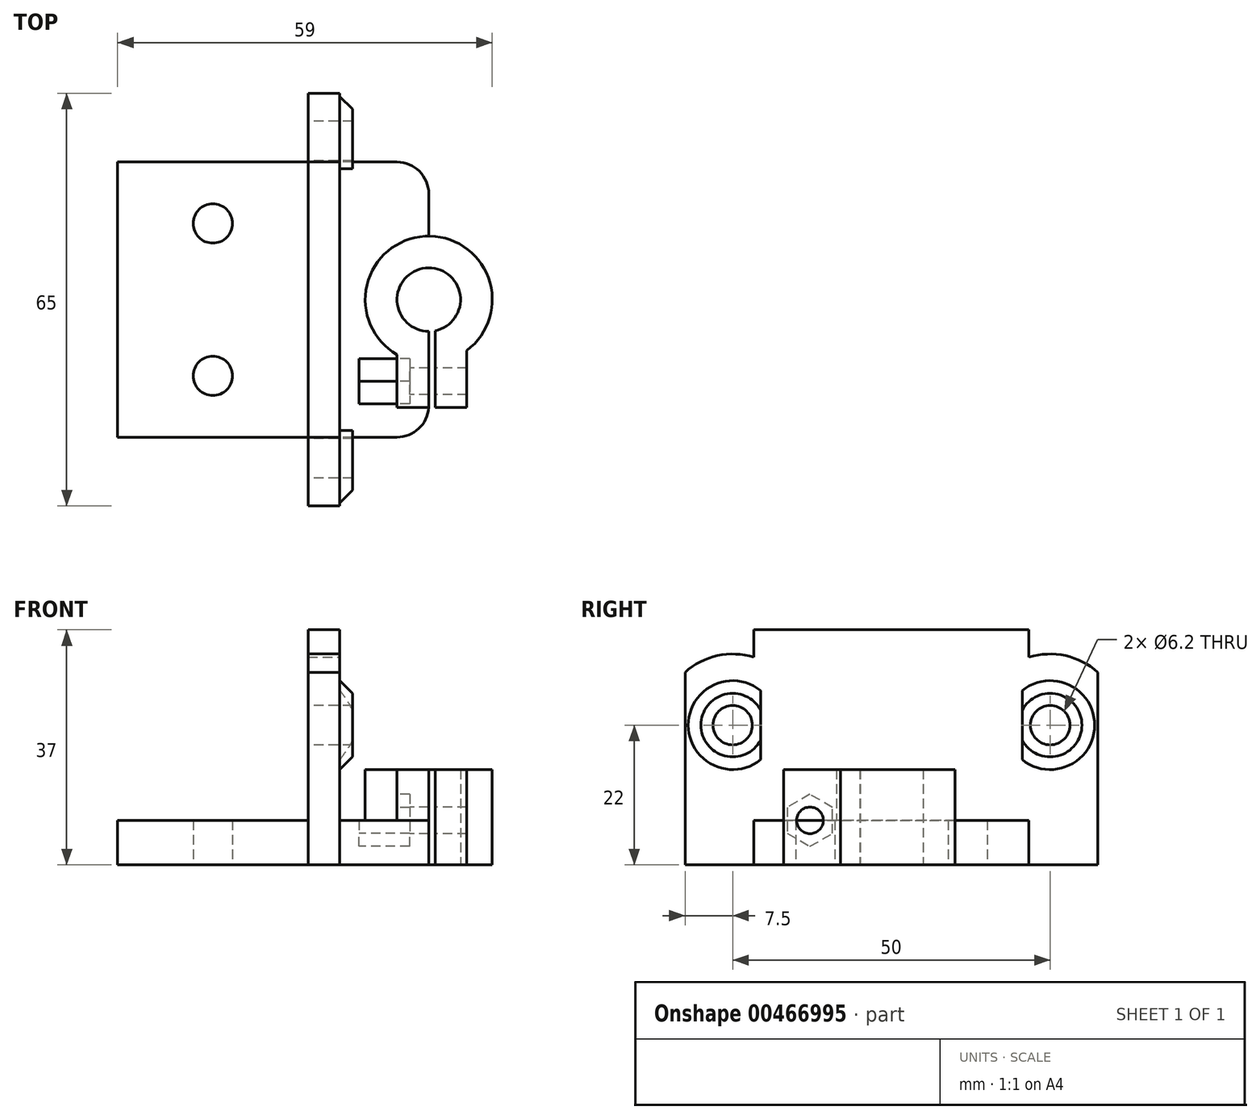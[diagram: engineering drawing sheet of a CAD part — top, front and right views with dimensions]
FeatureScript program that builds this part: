
annotation { "Feature Type Name" : "Feature", "Feature Type Description" : "" }
export const myFeature = defineFeature(function(context is Context, id is Id, definition is map)
    precondition{}
    {
        {
            var Q0;
            Q0=qCreatedBy(makeId("Top.planeOp"),FACE);
            var sketch = newSketch(context, id + "F0", { "sketchPlane" : qUnion([Q0])});
            skArc(sketch, "E0", {"start": v(1, -4.9) * mm, "mid": v(-0.5, 4.97) * mm, "end": v(0, -5) * mm});
            skArc(sketch, "E1", {"start": v(6, -8) * mm, "mid": v(-0.6, 9.98) * mm, "end": v(-5, -8.66) * mm});
            skCircle(sketch, "E2", {"center": v(-34, 12) * mm, "radius": 3.1 * mm});
            skCircle(sketch, "E3.MirrorC", {"center": v(-34, -12) * mm, "radius": 3.1 * mm});
            skLineSegment(sketch, "E4", {"start": v(0, 10) * mm, "end": v(0, 16.66) * mm});
            skLineSegment(sketch, "E5", {"start": v(-5, 21.66) * mm, "end": v(-49, 21.66) * mm});
            skLineSegment(sketch, "E6", {"start": v(-49, 21.66) * mm, "end": v(-49, 0) * mm});
            skPoint(sketch, "E7.visualSharp", {"position": v(0, 21.66) * mm});
            skArc(sketch, "E7.filletArc", {"start": v(0, 16.66) * mm, "mid": v(-1.46, 20.2) * mm, "end": v(-5, 21.66) * mm});
            skLineSegment(sketch, "E8.MirrorCS", {"start": v(-49, -21.66) * mm, "end": v(-49, 0) * mm});
            skLineSegment(sketch, "E9.MirrorCS", {"start": v(-5, -21.66) * mm, "end": v(-49, -21.66) * mm});
            skArc(sketch, "E10.MirrorCS", {"start": v(0, -16.66) * mm, "mid": v(-1.46, -20.2) * mm, "end": v(-5, -21.66) * mm});
            skLineSegment(sketch, "E11.MirrorCS", {"start": v(0, -10) * mm, "end": v(0, -16.66) * mm});
            skLineSegment(sketch, "E12", {"start": v(0, -5) * mm, "end": v(0, -10) * mm});
            skLineSegment(sketch, "E13", {"start": v(1, -9.95) * mm, "end": v(1, -4.9) * mm});
            skLineSegment(sketch, "E14", {"start": v(1, -9.95) * mm, "end": v(1, -17) * mm});
            skLineSegment(sketch, "E15", {"start": v(1, -17) * mm, "end": v(6, -17) * mm});
            skLineSegment(sketch, "E16", {"start": v(6, -17) * mm, "end": v(6, -8) * mm});
            skLineSegment(sketch, "E17", {"start": v(-5, -17) * mm, "end": v(-5, -8.66) * mm});
            skLineSegment(sketch, "E18", {"start": v(0, -17) * mm, "end": v(-5, -17) * mm});
            skSolve(sketch);
        }
        {
            var Q0;
            Q0=makeQuery(id+"F0.imprint","IMPRINT",FACE,{"disambiguationData":[TD([[makeQuery(id+"F0.imprint","IMPRINT",EDGE,{"derivedFrom":sQuery(id+"F0.wireOp",EDGE,"E2")}),-1.0]])]});
            extrude(context, id + "F1", {"entities" : qUnion([Q0]), "depth" : 7 * mm});
        }
        {
            var Q0;
            Q0=makeQuery(id+"F0.imprint","IMPRINT",FACE,{"disambiguationData":[TD([[makeQuery(id+"F0.imprint","IMPRINT",EDGE,{"derivedFrom":sQuery(id+"F0.wireOp",EDGE,"E0")}),-1.0]])]});
            extrude(context, id + "F2", {"entities" : qUnion([Q0]), "operationType" : NewBodyOperationType.ADD, "depth" : 15 * mm});
        }
        {
            var Q0;
            Q0=makeQuery(id+"F2.opExtrude","SWEPT_FACE",FACE,{"disambiguationData":[OSD([sQuery(id+"F0.wireOp",EDGE,"E17")])]});
            var sketch = newSketch(context, id + "F3", { "sketchPlane" : qUnion([Q0])});
            skCircle(sketch, "E19.cCircle", {"center": v(12.83, 7) * mm, "radius": 3.55 * mm, "construction": true});
            skLineSegment(sketch, "E19.0", {"start": v(16.38, 9.05) * mm, "end": v(16.38, 4.95) * mm});
            skLineSegment(sketch, "E19.1", {"start": v(16.38, 4.95) * mm, "end": v(12.83, 2.9) * mm});
            skLineSegment(sketch, "E19.2", {"start": v(12.83, 2.9) * mm, "end": v(9.28, 4.95) * mm});
            skLineSegment(sketch, "E19.3", {"start": v(9.28, 4.95) * mm, "end": v(9.28, 9.05) * mm});
            skLineSegment(sketch, "E19.4", {"start": v(9.28, 9.05) * mm, "end": v(12.83, 11.1) * mm});
            skLineSegment(sketch, "E19.5", {"start": v(12.83, 11.1) * mm, "end": v(16.38, 9.05) * mm});
            skPoint(sketch, "E19.0.midPoint", {"position": v(16.38, 7) * mm});
            skSolve(sketch);
        }
        {
            var Q0;
            Q0 = qSketchRegion(id + "F3", true);
            extrude(context, id + "F4", {"entities" : qUnion([Q0]), "operationType" : NewBodyOperationType.REMOVE, "oppositeDirection" : true, "depth" : 2 * mm, "hasSecondDirection" : true, "secondDirectionOppositeDirection" : false, "secondDirectionDepth" : 6 * mm});
        }
        {
            var Q0;
            Q0=makeQuery(id+"F2.opExtrude","SWEPT_FACE",FACE,{"disambiguationData":[OSD([sQuery(id+"F0.wireOp",EDGE,"E17")])]});
            var sketch = newSketch(context, id + "F5", { "sketchPlane" : qUnion([Q0])});
            skCircle(sketch, "E20", {"center": v(12.83, 7) * mm, "radius": 2.1 * mm});
            skSolve(sketch);
        }
        {
            var Q0;
            Q0 = qSketchRegion(id + "F5", true);
            extrude(context, id + "F6", {"entities" : qUnion([Q0]), "operationType" : NewBodyOperationType.REMOVE, "oppositeDirection" : true, "depth" : 25 * mm});
        }
        {
            var Q0;
            Q0=makeQuery(id+"F1.opExtrude","CAP_FACE",FACE,{"disambiguationData":[OSD([sQuery(id+"F0.wireOp",EDGE,"E1"),sQuery(id+"F0.wireOp",EDGE,"E2"),sQuery(id+"F0.wireOp",EDGE,"E3.MirrorC"),sQuery(id+"F0.wireOp",EDGE,"E4"),sQuery(id+"F0.wireOp",EDGE,"E5"),sQuery(id+"F0.wireOp",EDGE,"E6"),sQuery(id+"F0.wireOp",EDGE,"E7.filletArc"),sQuery(id+"F0.wireOp",EDGE,"E8.MirrorCS"),sQuery(id+"F0.wireOp",EDGE,"E9.MirrorCS"),sQuery(id+"F0.wireOp",EDGE,"E10.MirrorCS"),sQuery(id+"F0.wireOp",EDGE,"E17"),sQuery(id+"F0.wireOp",EDGE,"E18")])],"isStart":false});
            var sketch = newSketch(context, id + "F7", { "sketchPlane" : qUnion([Q0])});
            skLineSegment(sketch, "E21", {"start": v(-19, 21.66) * mm, "end": v(-19, -21.66) * mm});
            skLineSegment(sketch, "E22", {"start": v(-14, -21.66) * mm, "end": v(-14, 21.66) * mm});
            skLineSegment(sketch, "E23", {"start": v(-14, 21.66) * mm, "end": v(-14, 32.5) * mm});
            skLineSegment(sketch, "E24", {"start": v(-14, 32.5) * mm, "end": v(-19, 32.5) * mm});
            skLineSegment(sketch, "E25", {"start": v(-19, 32.5) * mm, "end": v(-19, 21.66) * mm});
            skLineSegment(sketch, "E26.MirrorCS", {"start": v(-14, -32.5) * mm, "end": v(-19, -32.5) * mm});
            skLineSegment(sketch, "E27.MirrorCS", {"start": v(-14, -21.66) * mm, "end": v(-14, -32.5) * mm});
            skLineSegment(sketch, "E28.MirrorCS", {"start": v(-19, -32.5) * mm, "end": v(-19, -21.66) * mm});
            skPoint(sketch, "E29.MirrorCS.start.orphan", {"position": v(-14, -21.66) * mm});
            skSolve(sketch);
        }
        {
            var Q0;
            Q0 = qSketchRegion(id + "F7", true);
            extrude(context, id + "F8", {"entities" : qUnion([Q0]), "operationType" : NewBodyOperationType.ADD, "depth" : 30 * mm});
        }
        {
            var Q0;
            Q0 = qSketchRegion(id + "F7", true);
            var Q1;
            {var subQ0=sQuery(id+"F0.wireOp",EDGE,"E18");var subQ1=sQuery(id+"F0.wireOp",EDGE,"E17");var subQ2=sQuery(id+"F0.wireOp",EDGE,"E10.MirrorCS");var subQ3=sQuery(id+"F0.wireOp",EDGE,"E1");Q1=makeQuery(id+"F2.boolean.opBoolean","MERGE",FACE,{"derivedFrom":[makeQuery(id+"F1.opExtrude","CAP_FACE",FACE,{"disambiguationData":[OSD([subQ3,sQuery(id+"F0.wireOp",EDGE,"E2"),sQuery(id+"F0.wireOp",EDGE,"E3.MirrorC"),sQuery(id+"F0.wireOp",EDGE,"E4"),sQuery(id+"F0.wireOp",EDGE,"E5"),sQuery(id+"F0.wireOp",EDGE,"E6"),sQuery(id+"F0.wireOp",EDGE,"E7.filletArc"),sQuery(id+"F0.wireOp",EDGE,"E8.MirrorCS"),sQuery(id+"F0.wireOp",EDGE,"E9.MirrorCS"),subQ2,subQ1,subQ0])],"isStart":true}),makeQuery(id+"F2.opExtrude","CAP_FACE",FACE,{"disambiguationData":[OSD([sQuery(id+"F0.wireOp",EDGE,"E0"),subQ3,subQ2,sQuery(id+"F0.wireOp",EDGE,"E11.MirrorCS"),sQuery(id+"F0.wireOp",EDGE,"E12"),sQuery(id+"F0.wireOp",EDGE,"E13"),sQuery(id+"F0.wireOp",EDGE,"E14"),sQuery(id+"F0.wireOp",EDGE,"E15"),sQuery(id+"F0.wireOp",EDGE,"E16"),subQ1,subQ0])],"isStart":true})]});}
            extrude(context, id + "F9", {"entities" : qUnion([Q0]), "operationType" : NewBodyOperationType.ADD, "depth" : 25 * mm, "hasSecondDirection" : true, "secondDirectionBound" : SecondDirectionBoundingType.UP_TO_SURFACE, "secondDirectionOppositeDirection" : true, "secondDirectionBoundEntityFace" : qUnion([Q1]), "secondDirectionDepth" : 25 * mm});
        }
        {
            var Q0;
            Q0=makeQuery(id+"F8.opExtrude","SWEPT_FACE",FACE,{"disambiguationData":[OSD([sQuery(id+"F7.wireOp",EDGE,"E21")])]});
            var sketch = newSketch(context, id + "F10", { "sketchPlane" : qUnion([Q0])});
            skCircle(sketch, "E30", {"center": v(-25, 22) * mm, "radius": 3.1 * mm});
            skCircle(sketch, "E31.MirrorC", {"center": v(25, 22) * mm, "radius": 3.1 * mm});
            skLineSegment(sketch, "E32", {"start": v(20, 43.23) * mm, "end": v(20, 10) * mm, "construction": true});
            skSolve(sketch);
        }
        {
            var Q0;
            Q0 = qSketchRegion(id + "F10", true);
            extrude(context, id + "F11", {"entities" : qUnion([Q0]), "operationType" : NewBodyOperationType.REMOVE, "oppositeDirection" : true, "depth" : 25 * mm});
        }
        {
            var Q0;
            {var subQ0=sQuery(id+"F7.wireOp",EDGE,"E28.MirrorCS");var subQ1=sQuery(id+"F7.wireOp",EDGE,"E25");var subQ2=sQuery(id+"F7.wireOp",EDGE,"E21");Q0=makeQuery(id+"F9.boolean.opBoolean","MERGE",FACE,{"derivedFrom":[makeQuery(id+"F8.opExtrude","SWEPT_FACE",FACE,{"disambiguationData":[OSD([subQ2,subQ1,subQ0])]}),makeQuery(id+"F9.opExtrude","SWEPT_FACE",FACE,{"disambiguationData":[OSD([subQ2,subQ1,subQ0])]})]});}
            var sketch = newSketch(context, id + "F12", { "sketchPlane" : qUnion([Q0])});
            skLineSegment(sketch, "E33", {"start": v(20, 49.57) * mm, "end": v(20, 11.1) * mm, "construction": true});
            skCircle(sketch, "E34", {"center": v(25, 22) * mm, "radius": 5 * mm});
            skCircle(sketch, "E35.MirrorC", {"center": v(-25, 22) * mm, "radius": 5 * mm});
            skCircle(sketch, "E36", {"center": v(25, 22) * mm, "radius": 3.1 * mm});
            skCircle(sketch, "E37.MirrorC", {"center": v(-25, 22) * mm, "radius": 3.1 * mm});
            skSolve(sketch);
        }
        {
            var Q0;
            Q0 = qSketchRegion(id + "F12", true);
            extrude(context, id + "F13", {"entities" : qUnion([Q0]), "operationType" : NewBodyOperationType.ADD, "oppositeDirection" : true, "depth" : 7 * mm});
        }
        {
            var Q0;
            {var subQ0=sQuery(id+"F7.wireOp",EDGE,"E27.MirrorCS");var subQ1=sQuery(id+"F7.wireOp",EDGE,"E23");var subQ2=sQuery(id+"F7.wireOp",EDGE,"E22");Q0=makeQuery(id+"F13.boolean.opBoolean","INTERSECT",EDGE,{"derivedFrom":[makeQuery(id+"F9.boolean.opBoolean","MERGE",FACE,{"derivedFrom":[makeQuery(id+"F8.opExtrude","SWEPT_FACE",FACE,{"disambiguationData":[OSD([subQ2,subQ1,subQ0])]}),makeQuery(id+"F9.opExtrude","SWEPT_FACE",FACE,{"disambiguationData":[OSD([subQ2,subQ1,subQ0])]})]}),makeQuery(id+"F13.opExtrude","SWEPT_FACE",FACE,{"disambiguationData":[OSD([sQuery(id+"F12.wireOp",EDGE,"E35.MirrorC")])]})]});}
            var Q1;
            {var subQ0=sQuery(id+"F7.wireOp",EDGE,"E27.MirrorCS");var subQ1=sQuery(id+"F7.wireOp",EDGE,"E23");var subQ2=sQuery(id+"F7.wireOp",EDGE,"E22");Q1=makeQuery(id+"F13.boolean.opBoolean","INTERSECT",EDGE,{"derivedFrom":[makeQuery(id+"F9.boolean.opBoolean","MERGE",FACE,{"derivedFrom":[makeQuery(id+"F8.opExtrude","SWEPT_FACE",FACE,{"disambiguationData":[OSD([subQ2,subQ1,subQ0])]}),makeQuery(id+"F9.opExtrude","SWEPT_FACE",FACE,{"disambiguationData":[OSD([subQ2,subQ1,subQ0])]})]}),makeQuery(id+"F13.opExtrude","SWEPT_FACE",FACE,{"disambiguationData":[OSD([sQuery(id+"F12.wireOp",EDGE,"E34")])]})]});}
            chamfer(context, id + "F14", {"entities" : qUnion([Q0, Q1]), "width" : 2 * mm, "tangentPropagation" : true});
        }
        {
            var Q0;
            {var subQ0=sQuery(id+"F7.wireOp",EDGE,"E27.MirrorCS");var subQ1=sQuery(id+"F7.wireOp",EDGE,"E23");var subQ2=sQuery(id+"F7.wireOp",EDGE,"E22");Q0=makeQuery(id+"F9.boolean.opBoolean","MERGE",FACE,{"derivedFrom":[makeQuery(id+"F8.opExtrude","SWEPT_FACE",FACE,{"disambiguationData":[OSD([subQ2,subQ1,subQ0])]}),makeQuery(id+"F9.opExtrude","SWEPT_FACE",FACE,{"disambiguationData":[OSD([subQ2,subQ1,subQ0])]})]});}
            var sketch = newSketch(context, id + "F15", { "sketchPlane" : qUnion([Q0])});
            skLineSegment(sketch, "E38", {"start": v(20.6, 14.46) * mm, "end": v(20.6, 30.1) * mm});
            skLineSegment(sketch, "E39", {"start": v(20.6, 30.1) * mm, "end": v(17.14, 30.1) * mm});
            skLineSegment(sketch, "E40", {"start": v(17.14, 30.1) * mm, "end": v(17.14, 14.46) * mm});
            skLineSegment(sketch, "E41", {"start": v(17.14, 14.46) * mm, "end": v(20.6, 14.46) * mm});
            skLineSegment(sketch, "E42.MirrorCS", {"start": v(-20.6, 30.1) * mm, "end": v(-17.14, 30.1) * mm});
            skLineSegment(sketch, "E43.MirrorCS", {"start": v(-17.14, 14.46) * mm, "end": v(-20.6, 14.46) * mm});
            skLineSegment(sketch, "E44.MirrorCS", {"start": v(-17.14, 30.1) * mm, "end": v(-17.14, 14.46) * mm});
            skLineSegment(sketch, "E45.MirrorCS", {"start": v(-20.6, 14.46) * mm, "end": v(-20.6, 30.1) * mm});
            skSolve(sketch);
        }
        {
            var Q0;
            Q0 = qSketchRegion(id + "F15", true);
            extrude(context, id + "F16", {"entities" : qUnion([Q0]), "operationType" : NewBodyOperationType.REMOVE, "depth" : 25 * mm});
        }
        {
            var Q0;
            {var subQ0=sQuery(id+"F7.wireOp",EDGE,"E27.MirrorCS");var subQ1=sQuery(id+"F7.wireOp",EDGE,"E23");var subQ2=sQuery(id+"F7.wireOp",EDGE,"E22");Q0=makeQuery(id+"F16.boolean.opBoolean","MERGE",FACE,{"derivedFrom":[makeQuery(id+"F9.boolean.opBoolean","MERGE",FACE,{"derivedFrom":[makeQuery(id+"F8.opExtrude","SWEPT_FACE",FACE,{"disambiguationData":[OSD([subQ2,subQ1,subQ0])]}),makeQuery(id+"F9.opExtrude","SWEPT_FACE",FACE,{"disambiguationData":[OSD([subQ2,subQ1,subQ0])]})]}),makeQuery(id+"F16.opExtrude","CAP_FACE",FACE,{"disambiguationData":[OSD([sQuery(id+"F15.wireOp",EDGE,"E38"),sQuery(id+"F15.wireOp",EDGE,"E39"),sQuery(id+"F15.wireOp",EDGE,"E40"),sQuery(id+"F15.wireOp",EDGE,"E41")])],"isStart":true}),makeQuery(id+"F16.opExtrude","CAP_FACE",FACE,{"disambiguationData":[OSD([sQuery(id+"F15.wireOp",EDGE,"E42.MirrorCS"),sQuery(id+"F15.wireOp",EDGE,"E43.MirrorCS"),sQuery(id+"F15.wireOp",EDGE,"E44.MirrorCS"),sQuery(id+"F15.wireOp",EDGE,"E45.MirrorCS")])],"isStart":true})]});}
            var sketch = newSketch(context, id + "F17", { "sketchPlane" : qUnion([Q0])});
            skLineSegment(sketch, "E46", {"start": v(21.66, 32.69) * mm, "end": v(21.66, 43.29) * mm});
            skArc(sketch, "E47", {"start": v(32.5, 30.31) * mm, "mid": v(27.4, 32.94) * mm, "end": v(21.66, 32.69) * mm});
            skLineSegment(sketch, "E48", {"start": v(32.5, 30.31) * mm, "end": v(32.5, 43.29) * mm});
            skLineSegment(sketch, "E49", {"start": v(32.5, 43.29) * mm, "end": v(21.66, 43.29) * mm});
            skPoint(sketch, "E50.orphan", {"position": v(21.66, 30.93) * mm});
            skPoint(sketch, "E51.MirrorP", {"position": v(-21.66, 30.93) * mm});
            skLineSegment(sketch, "E52.MirrorCS", {"start": v(-21.66, 32.69) * mm, "end": v(-21.66, 43.29) * mm});
            skArc(sketch, "E53.MirrorCS", {"start": v(-32.5, 30.31) * mm, "mid": v(-27.4, 32.94) * mm, "end": v(-21.66, 32.69) * mm});
            skLineSegment(sketch, "E54.MirrorCS", {"start": v(-32.5, 43.29) * mm, "end": v(-21.66, 43.29) * mm});
            skLineSegment(sketch, "E55.MirrorCS", {"start": v(-32.5, 30.31) * mm, "end": v(-32.5, 43.29) * mm});
            skSolve(sketch);
        }
        {
            var Q0;
            Q0 = qSketchRegion(id + "F17", true);
            extrude(context, id + "F18", {"entities" : qUnion([Q0]), "operationType" : NewBodyOperationType.REMOVE, "oppositeDirection" : true, "depth" : 25 * mm});
        }
    });
